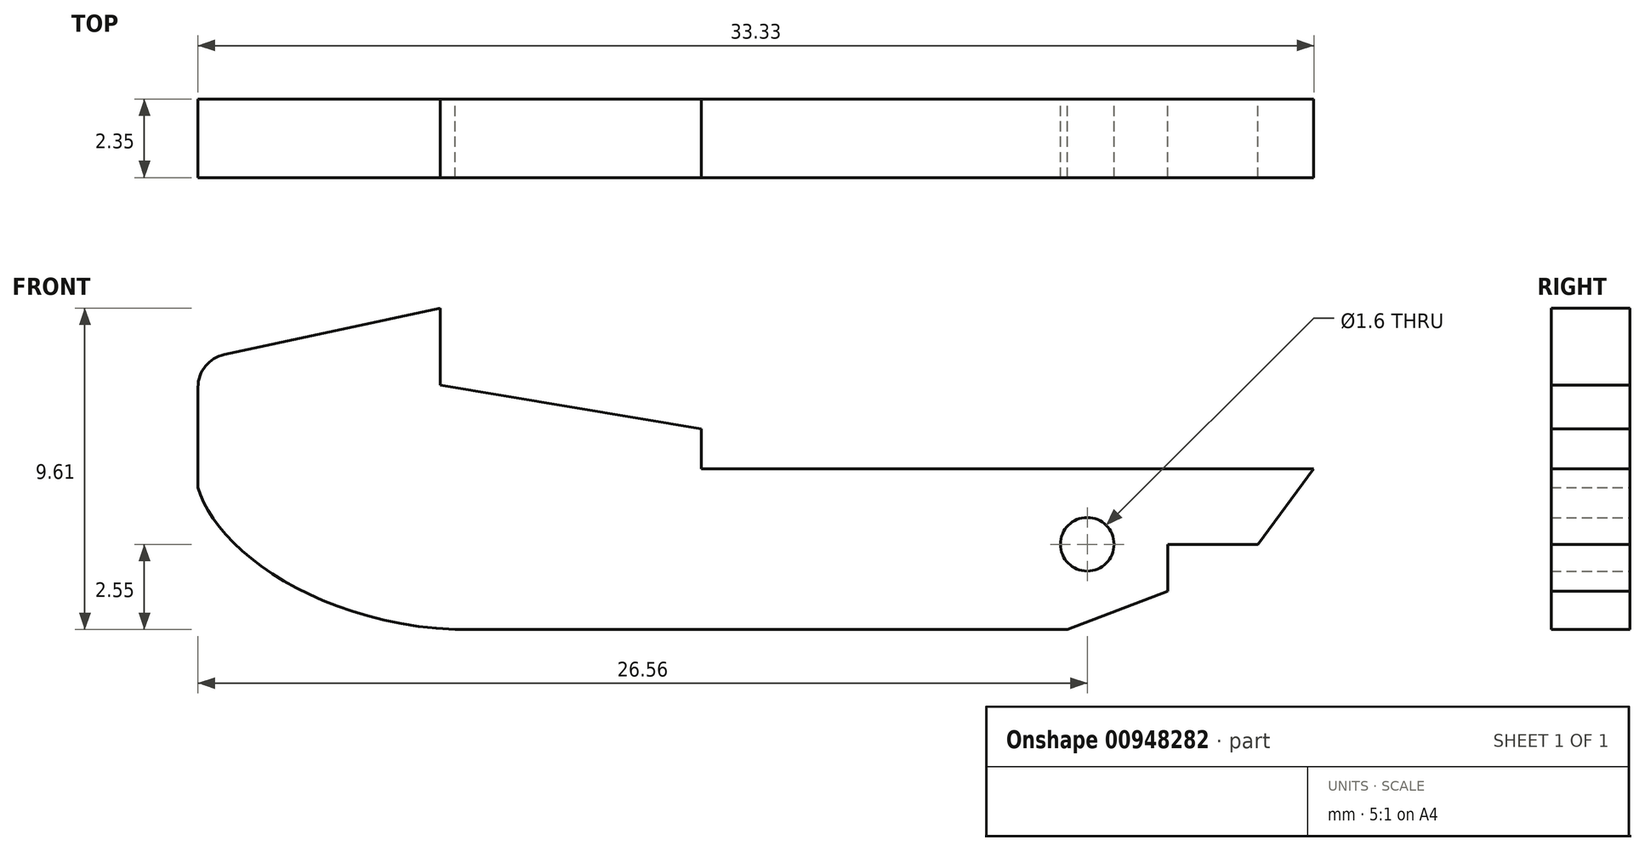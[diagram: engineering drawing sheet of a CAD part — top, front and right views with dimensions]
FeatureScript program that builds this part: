
annotation { "Feature Type Name" : "Feature", "Feature Type Description" : "" }
export const myFeature = defineFeature(function(context is Context, id is Id, definition is map)
    precondition{}
    {
        {
            var Q0;
            Q0=qCreatedBy(makeId("Front.planeOp"),FACE);
            var sketch = newSketch(context, id + "F0", { "sketchPlane" : qUnion([Q0])});
            skCircle(sketch, "E0", {"center": v(0, 0) * mm, "radius": 0.8 * mm});
            skLineSegment(sketch, "E1", {"start": v(-11.53, 2.25) * mm, "end": v(6.77, 2.25) * mm});
            skLineSegment(sketch, "E2", {"start": v(2.4, 0) * mm, "end": v(2.4, -1.4) * mm});
            skLineSegment(sketch, "E3", {"start": v(2.4, -1.4) * mm, "end": v(-0.59, -2.55) * mm});
            skLineSegment(sketch, "E4", {"start": v(-0.59, -2.55) * mm, "end": v(-18.89, -2.55) * mm});
            skLineSegment(sketch, "E5", {"start": v(-11.53, 2.25) * mm, "end": v(-11.53, 3.45) * mm});
            skLineSegment(sketch, "E6", {"start": v(-11.53, 3.45) * mm, "end": v(-19.32, 4.76) * mm});
            skLineSegment(sketch, "E7", {"start": v(-19.32, 4.76) * mm, "end": v(-19.32, 7.06) * mm});
            skLineSegment(sketch, "E8", {"start": v(-19.32, 7.06) * mm, "end": v(-26.56, 5.5) * mm});
            skLineSegment(sketch, "E9", {"start": v(-26.56, 5.5) * mm, "end": v(-26.56, 1.7) * mm});
            skFitSpline(sketch, "E10", {"points": [v(-26.56, 1.7) * mm, v(-18.89, -2.55) * mm], "startDerivative": vector(1.3, -5.13) * mm, "endDerivative": vector(12.9, -0.6) * mm});
            skLineSegment(sketch, "E11", {"start": v(2.4, 0) * mm, "end": v(5.1, 0) * mm});
            skLineSegment(sketch, "E12", {"start": v(5.1, 0) * mm, "end": v(6.77, 2.25) * mm});
            skSolve(sketch);
        }
        {
            var Q0;
            Q0=makeQuery(id+"F0.imprint","IMPRINT",FACE,{"disambiguationData":[TD([[makeQuery(id+"F0.imprint","IMPRINT",EDGE,{"derivedFrom":sQuery(id+"F0.wireOp",EDGE,"E0")}),-1.0]])]});
            extrude(context, id + "F1", {"entities" : qUnion([Q0]), "depth" : 2.35 * mm, "offsetDistance" : 25 * mm});
        }
        {
            var Q0;
            Q0=makeQuery(id+"F1.opExtrude","SWEPT_EDGE",EDGE,{"disambiguationData":[OSD([sQuery(id+"F0.wireOp",EDGE,"E8"),sQuery(id+"F0.wireOp",EDGE,"E9")])]});
            fillet(context, id + "F2", {"entities" : qUnion([Q0]), "radius" : 1 * mm, "tangentPropagation" : true, "allowEdgeOverflow" : false});
        }
    });
